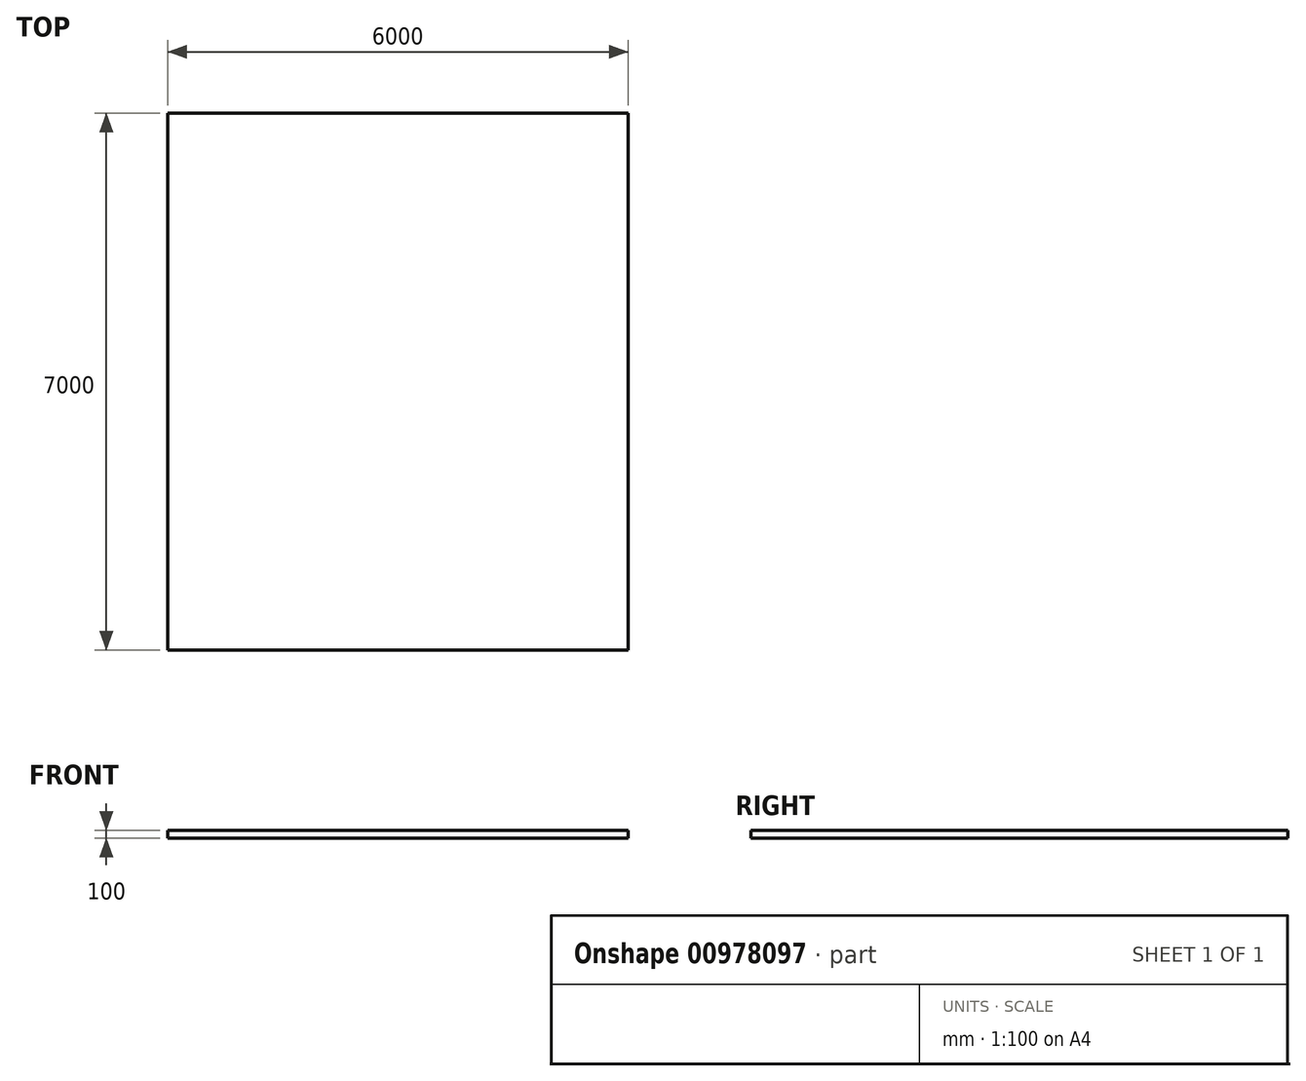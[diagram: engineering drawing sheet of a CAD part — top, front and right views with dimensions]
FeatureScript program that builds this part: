
annotation { "Feature Type Name" : "Feature", "Feature Type Description" : "" }
export const myFeature = defineFeature(function(context is Context, id is Id, definition is map)
    precondition{}
    {
        {
            var Q0;
            Q0=qCreatedBy(makeId("Top.planeOp"),FACE);
            var sketch = newSketch(context, id + "F0", { "sketchPlane" : qUnion([Q0])});
            skLineSegment(sketch, "E0.bottom", {"start": v(3000, -3500) * mm, "end": v(-3000, -3500) * mm});
            skLineSegment(sketch, "E0.top", {"start": v(3000, 3500) * mm, "end": v(-3000, 3500) * mm});
            skLineSegment(sketch, "E0.left", {"start": v(3000, -3500) * mm, "end": v(3000, 3500) * mm});
            skLineSegment(sketch, "E0.right", {"start": v(-3000, -3500) * mm, "end": v(-3000, 3500) * mm});
            skPoint(sketch, "E0.middle", {"position": v(0, 0) * mm});
            skSolve(sketch);
        }
        {
            var Q0;
            Q0=makeQuery(id+"F0.imprint","IMPRINT",FACE,{"disambiguationData":[TD([[makeQuery(id+"F0.imprint","IMPRINT",EDGE,{"derivedFrom":sQuery(id+"F0.wireOp",EDGE,"E0.bottom")}),-1.0]])]});
            extrude(context, id + "F1", {"entities" : qUnion([Q0]), "endBound" : BoundingType.SYMMETRIC, "depth" : 100 * mm, "offsetDistance" : 25 * mm});
        }
    });
